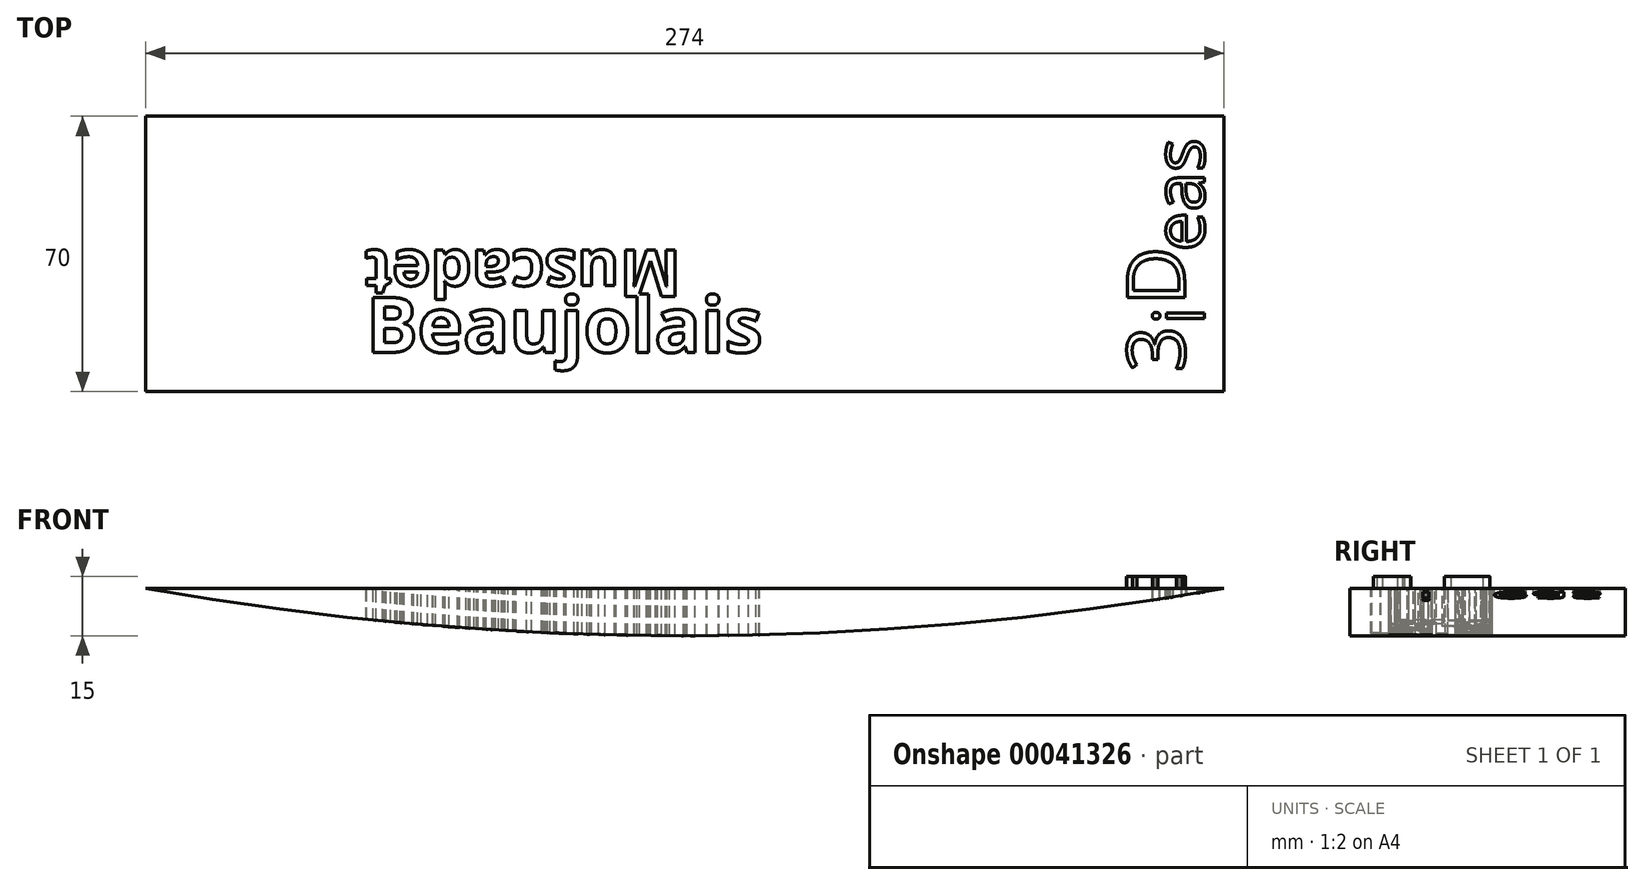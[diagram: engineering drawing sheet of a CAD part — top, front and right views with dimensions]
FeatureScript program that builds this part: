
annotation { "Feature Type Name" : "Feature", "Feature Type Description" : "" }
export const myFeature = defineFeature(function(context is Context, id is Id, definition is map)
    precondition{}
    {
        {
            var Q0;
            Q0=qCreatedBy(makeId("Top.planeOp"),FACE);
            var sketch = newSketch(context, id + "F0", { "sketchPlane" : qUnion([Q0])});
            skLineSegment(sketch, "E0.rect.bottom", {"start": v(-137, 35) * mm, "end": v(137, 35) * mm});
            skLineSegment(sketch, "E0.rect.top", {"start": v(-137, -35) * mm, "end": v(137, -35) * mm});
            skLineSegment(sketch, "E0.rect.left", {"start": v(-137, 35) * mm, "end": v(-137, -35) * mm});
            skLineSegment(sketch, "E0.rect.right", {"start": v(137, 35) * mm, "end": v(137, -35) * mm});
            skPoint(sketch, "E0.rect.middle", {"position": v(0, 0) * mm});
            skLineSegment(sketch, "E1", {"start": v(-81, 35) * mm, "end": v(-81, -35) * mm, "construction": true});
            skLineSegment(sketch, "E2", {"start": v(107.6, -35) * mm, "end": v(107.6, 35) * mm, "construction": true});
            skSolve(sketch);
        }
        {
            var Q0;
            Q0 = qSketchRegion(id + "F0", true);
            extrude(context, id + "F1", {"entities" : qUnion([Q0]), "depth" : 12 * mm});
        }
        {
            var Q0;
            Q0=makeQuery(id+"F1.opExtrude","CAP_FACE",FACE,{"disambiguationData":[OSD([sQuery(id+"F0.wireOp",EDGE,"E0.rect.bottom"),sQuery(id+"F0.wireOp",EDGE,"E0.rect.top"),sQuery(id+"F0.wireOp",EDGE,"E0.rect.left"),sQuery(id+"F0.wireOp",EDGE,"E0.rect.right")])],"isStart":false});
            var sketch = newSketch(context, id + "F2", { "sketchPlane" : qUnion([Q0])});
            skText(sketch, "E3", { "text": "3 D", "fontName": "OpenSans-Regular.ttf"});
            const initialGuessF2  = {"E3": [0.127, -0.03, 0, 1, 0.01468]};
            skSetInitialGuess(sketch, initialGuessF2);
            skSolve(sketch);
        }
        {
            var Q0;
            Q0 = qSketchRegion(id + "F2", true);
            extrude(context, id + "F3", {"entities" : qUnion([Q0]), "operationType" : NewBodyOperationType.ADD, "depth" : 3 * mm});
        }
        {
            var Q0;
            {var subQ0=sQuery(id+"F0.wireOp",EDGE,"E0.rect.bottom");var subQ1=sQuery(id+"F0.wireOp",EDGE,"E0.rect.top");var subQ2=sQuery(id+"F0.wireOp",EDGE,"E0.rect.left");var subQ3=sQuery(id+"F0.wireOp",EDGE,"E0.rect.right");Q0=makeQuery(id+"F3.boolean.opBoolean","SPLIT",FACE,{"disambiguationData":[TD([makeQuery(id+"F1.opExtrude","SWEPT_FACE",FACE,{"disambiguationData":[OSD([subQ0])]})])],"derivedFrom":makeQuery(id+"F1.opExtrude","CAP_FACE",FACE,{"disambiguationData":[OSD([subQ0,subQ1,subQ2,subQ3])],"isStart":false})});}
            var sketch = newSketch(context, id + "F4", { "sketchPlane" : qUnion([Q0])});
            skText(sketch, "E4", { "text": "i   eas", "fontName": "OpenSans-Regular.ttf"});
            const initialGuessF4  = {"E4": [0.132, -0.018, 0, 1, 0.013]};
            skSetInitialGuess(sketch, initialGuessF4);
            skSolve(sketch);
        }
        {
            var Q0;
            Q0 = qSketchRegion(id + "F4", true);
            extrude(context, id + "F5", {"entities" : qUnion([Q0]), "operationType" : NewBodyOperationType.REMOVE, "oppositeDirection" : true, "depth" : 3 * mm});
        }
        {
            var Q0;
            Q0=makeQuery(id+"F1.opExtrude","SWEPT_FACE",FACE,{"disambiguationData":[OSD([sQuery(id+"F0.wireOp",EDGE,"E0.rect.top")])]});
            var sketch = newSketch(context, id + "F6", { "sketchPlane" : qUnion([Q0])});
            skArc(sketch, "E5", {"start": v(-137, 12) * mm, "mid": v(0, 0) * mm, "end": v(137, 12) * mm});
            skSolve(sketch);
        }
        {
            var Q0;
            {var subQ0=sQuery(id+"F0.wireOp",EDGE,"E0.rect.top");var subQ4=makeQuery(id+"F1.opExtrude","SWEPT_EDGE",EDGE,{"disambiguationData":[OSD([subQ0,sQuery(id+"F0.wireOp",EDGE,"E0.rect.left")])]});Q0=makeQuery(id+"F6.imprint","IMPRINT",FACE,{"disambiguationData":[TD([[makeQuery(id+"F6.imprint","IMPRINT",EDGE,{"derivedFrom":subQ4}),1.0]])]});}
            var Q1;
            {var subQ0=sQuery(id+"F0.wireOp",EDGE,"E0.rect.top");var subQ4=makeQuery(id+"F1.opExtrude","SWEPT_EDGE",EDGE,{"disambiguationData":[OSD([subQ0,sQuery(id+"F0.wireOp",EDGE,"E0.rect.right")])]});Q1=makeQuery(id+"F6.imprint","IMPRINT",FACE,{"disambiguationData":[TD([[makeQuery(id+"F6.imprint","IMPRINT",EDGE,{"derivedFrom":subQ4}),-1.0]])]});}
            extrude(context, id + "F7", {"entities" : qUnion([Q0, Q1]), "operationType" : NewBodyOperationType.REMOVE, "endBound" : BoundingType.THROUGH_ALL, "oppositeDirection" : true, "depth" : 25 * mm});
        }
        {
            var Q0;
            {var subQ0=sQuery(id+"F0.wireOp",EDGE,"E0.rect.bottom");var subQ1=sQuery(id+"F0.wireOp",EDGE,"E0.rect.top");var subQ2=sQuery(id+"F0.wireOp",EDGE,"E0.rect.left");var subQ3=sQuery(id+"F0.wireOp",EDGE,"E0.rect.right");var subQ25=makeQuery(id+"F1.opExtrude","SWEPT_FACE",FACE,{"disambiguationData":[OSD([subQ0])]});Q0=makeQuery(id+"F5.boolean.opBoolean","SPLIT",FACE,{"disambiguationData":[TD([subQ25])],"derivedFrom":makeQuery(id+"F3.boolean.opBoolean","SPLIT",FACE,{"disambiguationData":[TD([subQ25])],"derivedFrom":makeQuery(id+"F1.opExtrude","CAP_FACE",FACE,{"disambiguationData":[OSD([subQ0,subQ1,subQ2,subQ3])],"isStart":false})})});}
            var sketch = newSketch(context, id + "F8", { "sketchPlane" : qUnion([Q0])});
            skText(sketch, "E6", { "text": "Beaujolais", "fontName": "OpenSans-Bold.ttf"});
            skText(sketch, "E7", { "text": "Muscadet", "fontName": "OpenSans-Bold.ttf"});
            const initialGuessF8  = {"E6": [-0.081, -0.025, 1, 0, 0.01406], "E7": [-0.001, 0.00096, -1, 0, 0.0119]};
            skSetInitialGuess(sketch, initialGuessF8);
            skSolve(sketch);
        }
        {
            var Q0;
            Q0 = qSketchRegion(id + "F8", true);
            extrude(context, id + "F9", {"entities" : qUnion([Q0]), "operationType" : NewBodyOperationType.REMOVE, "oppositeDirection" : true, "depth" : 25 * mm});
        }
    });
